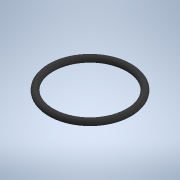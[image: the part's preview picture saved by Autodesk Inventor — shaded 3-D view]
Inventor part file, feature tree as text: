
AUTODESK INVENTOR PART (.ipt)
format: ipt  version: 2020 (Build 240168000, 168)  size: 122,368 bytes
history: native  units: mm
features: revolve x1, sketch x1
ambient origin geometry x8: Origin, YZ Plane, XZ Plane, XY Plane, X Axis, Y Axis, Z Axis, Center Point
bodies: Solid1 (feature_tree)
feature tree (2):
  revolve  "Revolution1"  [1 undecoded]
  sketch  "Sketch1"  dims[d0=1.78mm d1=11.065mm d2=90.0deg]
note: 1 required parameter value undecoded (feature->parameter linkage not recoverable at this tier; creation-order binding heuristic only, values carry confidence <= 0.55)
